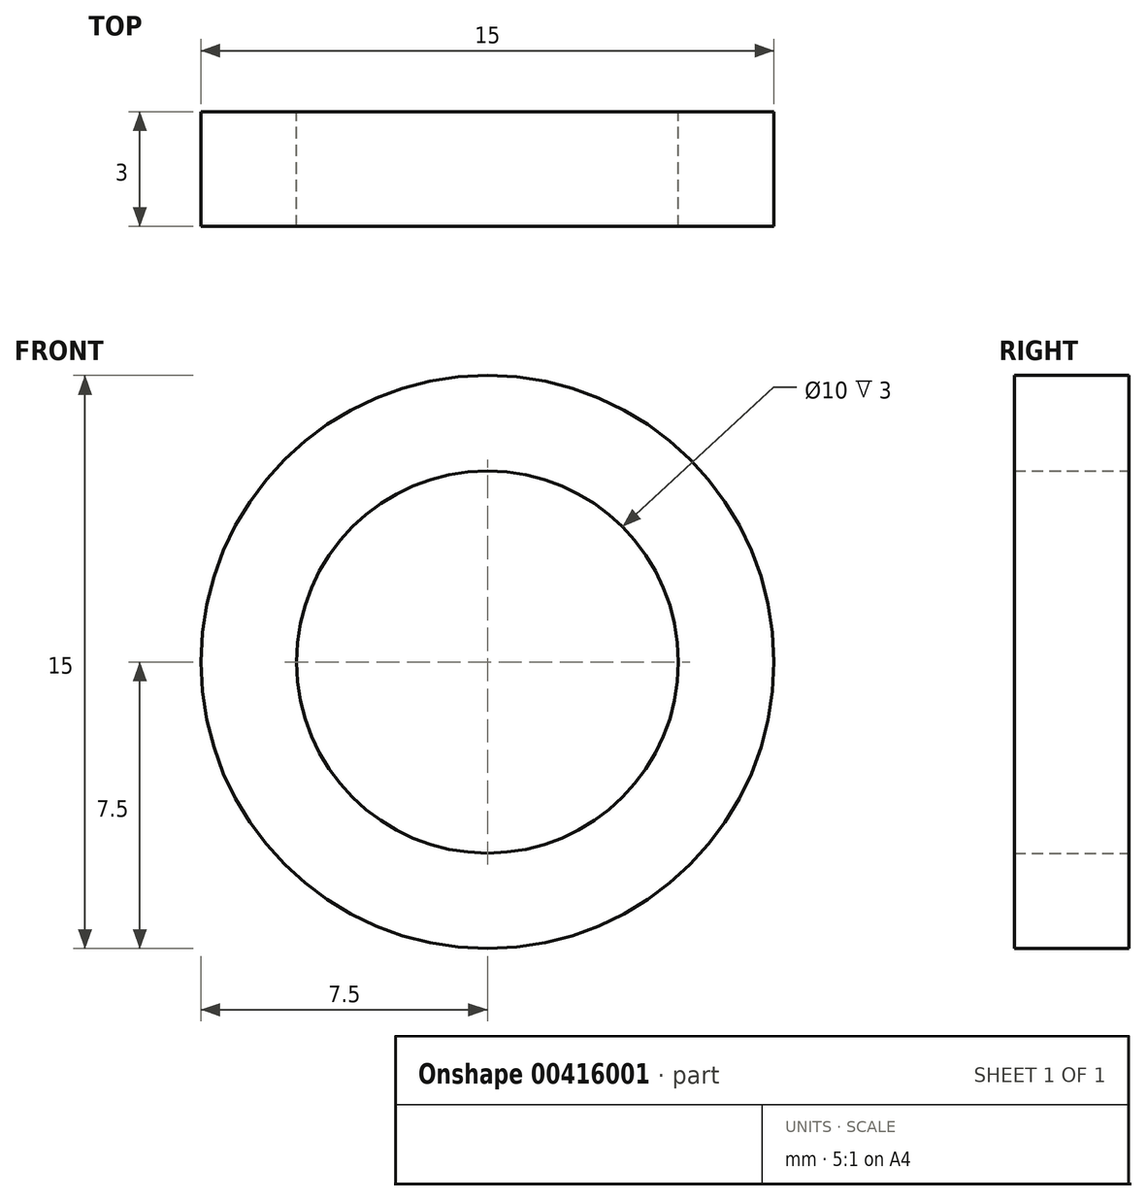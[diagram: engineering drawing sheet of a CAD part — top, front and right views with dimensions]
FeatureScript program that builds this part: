
annotation { "Feature Type Name" : "Feature", "Feature Type Description" : "" }
export const myFeature = defineFeature(function(context is Context, id is Id, definition is map)
    precondition{}
    {
        {
            var Q0;
            Q0=qCreatedBy(makeId("Front.planeOp"),FACE);
            var sketch = newSketch(context, id + "F0", { "sketchPlane" : qUnion([Q0])});
            skCircle(sketch, "E0", {"center": v(0, 0) * mm, "radius": 7.5 * mm});
            skCircle(sketch, "E1", {"center": v(0, 0) * mm, "radius": 5 * mm});
            skSolve(sketch);
        }
        {
            var Q0;
            Q0=makeQuery(id+"F0.imprint","IMPRINT",FACE,{"disambiguationData":[TD([[makeQuery(id+"F0.imprint","IMPRINT",EDGE,{"derivedFrom":sQuery(id+"F0.wireOp",EDGE,"E0")}),1.0]])]});
            extrude(context, id + "F1", {"entities" : qUnion([Q0]), "depth" : 3 * mm});
        }
    });
